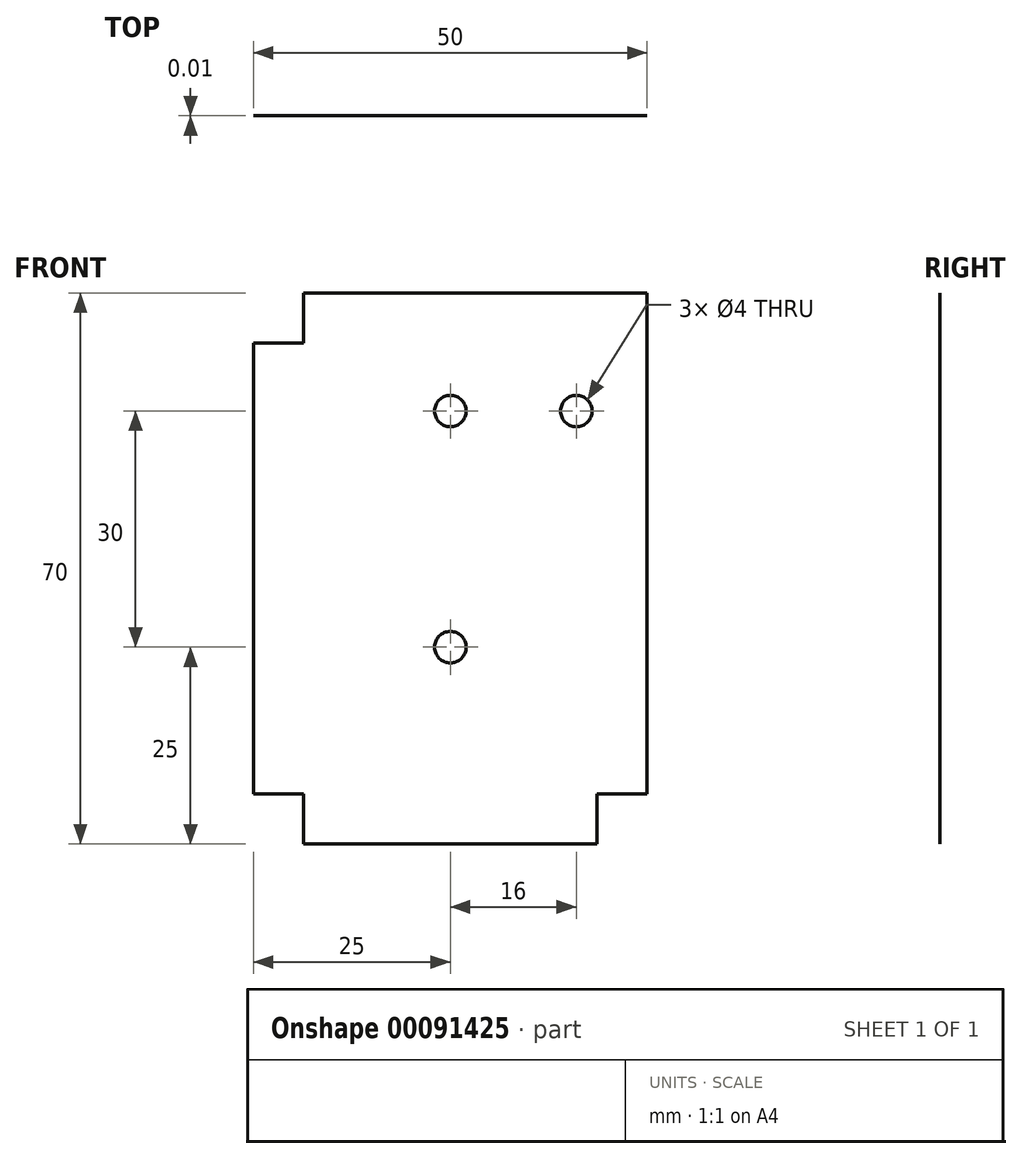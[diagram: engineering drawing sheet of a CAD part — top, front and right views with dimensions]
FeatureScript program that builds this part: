
annotation { "Feature Type Name" : "Feature", "Feature Type Description" : "" }
export const myFeature = defineFeature(function(context is Context, id is Id, definition is map)
    precondition{}
    {
        {
            var Q0;
            Q0=qCreatedBy(makeId("Front.planeOp"),FACE);
            var sketch = newSketch(context, id + "F0", { "sketchPlane" : qUnion([Q0])});
            skPoint(sketch, "E0", {"position": v(0, 0) * mm});
            skLineSegment(sketch, "E1", {"start": v(0, 48.44) * mm, "end": v(0, -58.78) * mm, "construction": true});
            skPoint(sketch, "E2", {"position": v(0, 30) * mm});
            skLineSegment(sketch, "E3", {"start": v(-47.56, 30) * mm, "end": v(45.6, 30) * mm, "construction": true});
            skPoint(sketch, "E4", {"position": v(16, 30) * mm});
            skLineSegment(sketch, "E5.bottom", {"start": v(-18.65, 45) * mm, "end": v(25, 45) * mm});
            skLineSegment(sketch, "E5.top", {"start": v(-18.65, -25) * mm, "end": v(18.65, -25) * mm});
            skLineSegment(sketch, "E5.left", {"start": v(-25, 30) * mm, "end": v(-25, -18.65) * mm});
            skLineSegment(sketch, "E5.right", {"start": v(25, 45) * mm, "end": v(25, -18.65) * mm});
            skCircle(sketch, "E6", {"center": v(16, 30) * mm, "radius": 2 * mm});
            skCircle(sketch, "E7", {"center": v(0, 30) * mm, "radius": 2 * mm});
            skCircle(sketch, "E8", {"center": v(0, 0) * mm, "radius": 2 * mm});
            skLineSegment(sketch, "E9", {"start": v(-25, -18.65) * mm, "end": v(-18.65, -18.65) * mm});
            skLineSegment(sketch, "E10", {"start": v(-18.65, -18.65) * mm, "end": v(-18.65, -25) * mm});
            skLineSegment(sketch, "E11", {"start": v(18.65, -25) * mm, "end": v(18.65, -18.65) * mm});
            skLineSegment(sketch, "E12", {"start": v(18.65, -18.65) * mm, "end": v(25, -18.65) * mm});
            skLineSegment(sketch, "E13", {"start": v(-25, 38.65) * mm, "end": v(-18.65, 38.65) * mm});
            skLineSegment(sketch, "E14", {"start": v(-18.65, 38.65) * mm, "end": v(-18.65, 45) * mm});
            skLineSegment(sketch, "E15", {"start": v(-25, 30) * mm, "end": v(-25, 38.65) * mm});
            skSolve(sketch);
        }
        {
            var Q0;
            Q0=makeQuery(id+"F0.imprint","IMPRINT",FACE,{"disambiguationData":[TD([[makeQuery(id+"F0.imprint","IMPRINT",EDGE,{"derivedFrom":sQuery(id+"F0.wireOp",EDGE,"E5.bottom")}),-1.0]])]});
            extrude(context, id + "F1", {"entities" : qUnion([Q0]), "depth" : 1 / 101.6 * mm});
        }
    });
